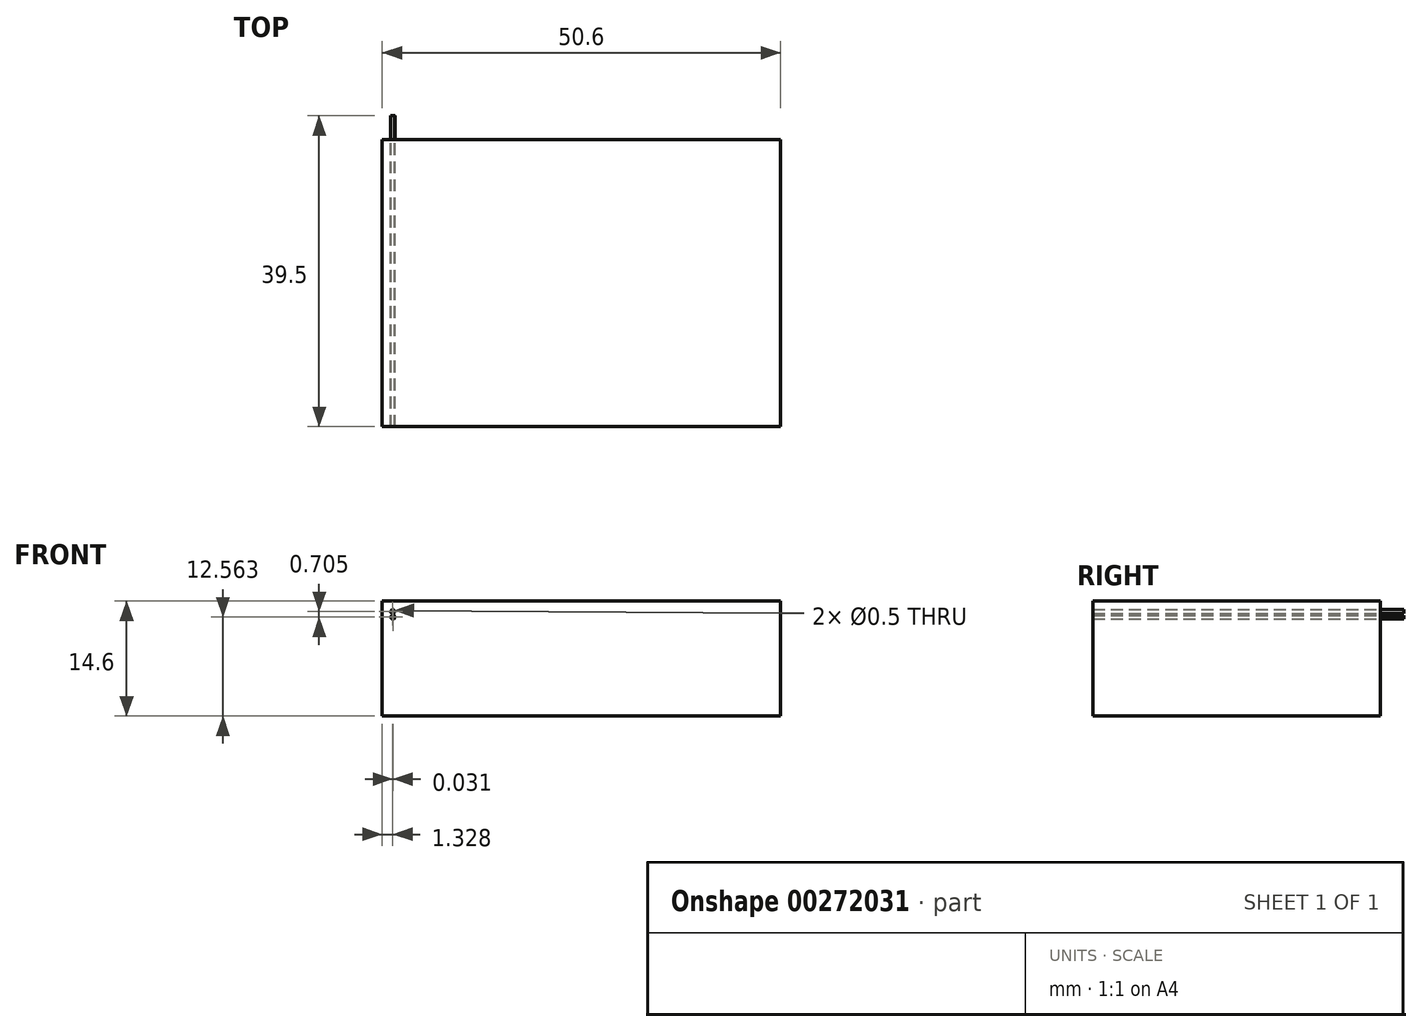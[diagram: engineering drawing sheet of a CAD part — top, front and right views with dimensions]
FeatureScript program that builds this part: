
annotation { "Feature Type Name" : "Feature", "Feature Type Description" : "" }
export const myFeature = defineFeature(function(context is Context, id is Id, definition is map)
    precondition{}
    {
        {
            var Q0;
            Q0=qCreatedBy(makeId("Front.planeOp"),FACE);
            var sketch = newSketch(context, id + "F0", { "sketchPlane" : qUnion([Q0])});
            skLineSegment(sketch, "E0", {"start": v(-25.3, 7.3) * mm, "end": v(-25.3, -7.3) * mm});
            skLineSegment(sketch, "E1", {"start": v(-25.3, -7.3) * mm, "end": v(25.3, -7.3) * mm});
            skLineSegment(sketch, "E2", {"start": v(25.3, -7.3) * mm, "end": v(25.3, 7.3) * mm});
            skLineSegment(sketch, "E3", {"start": v(25.3, 7.3) * mm, "end": v(-25.3, 7.3) * mm});
            skLineSegment(sketch, "E4", {"start": v(25.3, -7.3) * mm, "end": v(-25.3, 7.3) * mm, "construction": true});
            skLineSegment(sketch, "E5", {"start": v(-25.3, -7.3) * mm, "end": v(25.3, 7.3) * mm, "construction": true});
            skPoint(sketch, "E6", {"position": v(0, 0) * mm});
            skCircle(sketch, "E7", {"center": v(-23.97, 5.97) * mm, "radius": 0.25 * mm});
            skCircle(sketch, "E8", {"center": v(-23.94, 5.26) * mm, "radius": 0.25 * mm});
            skSolve(sketch);
        }
        {
            var Q0;
            Q0=makeQuery(id+"F0.imprint","IMPRINT",FACE,{"disambiguationData":[TD([[makeQuery(id+"F0.imprint","IMPRINT",EDGE,{"derivedFrom":sQuery(id+"F0.wireOp",EDGE,"E0")}),1.0]])]});
            extrude(context, id + "F1", {"entities" : qUnion([Q0]), "depth" : 36.5 * mm});
        }
        {
            var Q0;
            Q0=makeQuery(id+"F0.imprint","IMPRINT",FACE,{"disambiguationData":[TD([[makeQuery(id+"F0.imprint","IMPRINT",EDGE,{"derivedFrom":sQuery(id+"F0.wireOp",EDGE,"E7")}),1.0]])]});
            var Q1;
            Q1=makeQuery(id+"F0.imprint","IMPRINT",FACE,{"disambiguationData":[TD([[makeQuery(id+"F0.imprint","IMPRINT",EDGE,{"derivedFrom":sQuery(id+"F0.wireOp",EDGE,"E8")}),1.0]])]});
            extrude(context, id + "F2", {"entities" : qUnion([Q0, Q1]), "oppositeDirection" : true, "depth" : 3 * mm});
        }
    });
